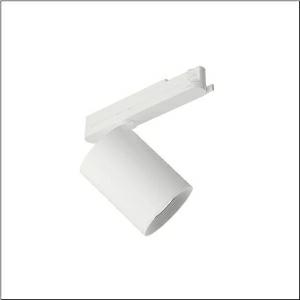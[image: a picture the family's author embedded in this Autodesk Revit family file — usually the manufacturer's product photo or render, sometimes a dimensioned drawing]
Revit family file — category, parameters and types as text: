
# Revit family: spot_11_51sd14mbd5a
name_source: partatom
category: Lighting Fixtures
units: mm (PartAtom-declared; Revit-internal decimal feet)

## family parameters
Cut with Voids When Loaded = No
Host = Face
Light Source = No
Part Type = Normal
Room Calculation Point = No
Round Connector Dimension = Use Diameter
Shared = No

## types (1)
- --- (1 x LED, 7420 lm, 50.3 W, 4000K)
    Apparent Load = 50 VA
    CIE Flux Codes = 95 98 100 100 100
    Color Rendering = 90
    Color Temperature = 4000K
    Default Elevation = 1800 mm
    Description = Spot 11, directional spotlight, light control with lens, of PMMA, LED rated luminous flux: 5.670lm, light colour: 940, control gear: ECG Multilumen, with 3-phase adapter, mains connection: 220..240V, AC, 50/60Hz, of aluminium, traffic white (RAL 9016), length: 213mm, diameter: 105mm, protection rating (complete): IP20, insulation class (complete): insulation class I (protective earthing), certification: CE, impact resistance: IK02, permissible ambient temperature for indoor applications: -20..+40°C, packaging unit: 1 piece
    Height = 175 mm
    Lamp = 1 x LED
    Lamp Light Flux = 7420 lm
    Lamp Power = 50.3 W
    Lamp count = 1
    Length = 105 mm
    Luminous efficacy = 148 lm/W
    Manufacturer = Siteco
    ModVariant = No
    Model = 51SD14MBD5A
    Mounting Place = Ceiling
    Mounting Type = Pendant
    Number of Poles = 1
    OnlyDefault = Yes
    Power Factor = 1
    Product Name = Spot 11
    Product group = directional spotlight
    ProductGroupID = 906
    Protection Class = Protection class I
    Protection Degree = IP 20
    RLX_Detail_Level = 1
    RLX_Emergency_Light_Flux = 0 lm
    RLX_Emergency_Type = 0
    RLX_Emergency_Type_DB = No
    RlxData = <blob elided: 17701 chars, md5=105e136e>
    Socket = socket
    Standby Power = 0 W
    System Light Flux = 7420 lm
    System Power = 50 W
    Type Comments = factory setting: luminous flux: 100 % | (ON | ON | ON | ON) | 1050 mA
    Type Image = l_1006697.jpg
    URL = http://relux.com
    VarID = @adj_147450
    Voltage = 0 V
    Weight = 0.00 kg
    Width = 0 mm  [stored 0 ft]

note: [stored X ft] marks values corroborated as IEEE doubles in the binary element streams (Revit-internal decimal feet)

## geometry (parser evidence)
native form markers: Blend x4, Sweep x12
no freeform markers — native parametric forms only
